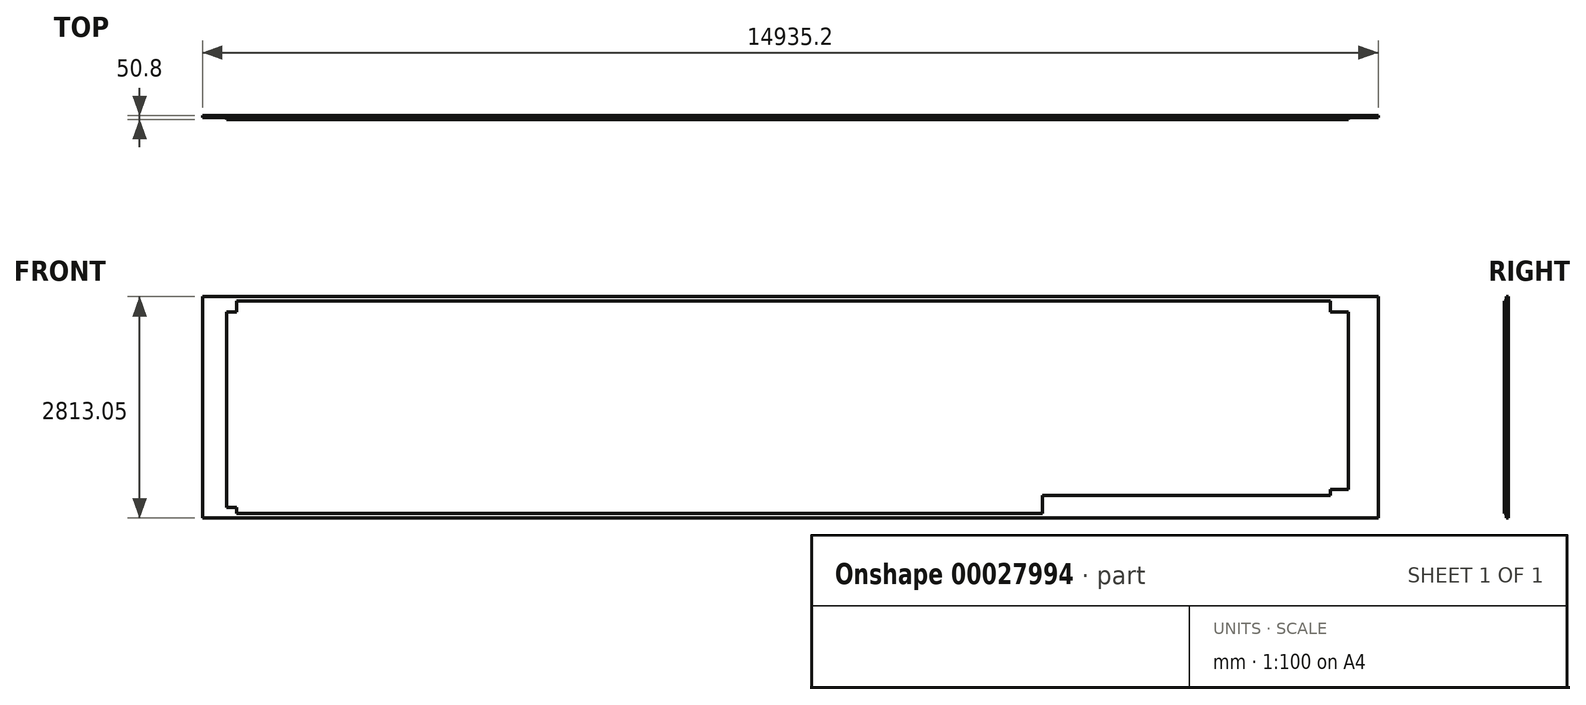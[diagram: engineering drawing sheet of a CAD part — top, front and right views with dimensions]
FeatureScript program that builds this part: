
annotation { "Feature Type Name" : "Feature", "Feature Type Description" : "" }
export const myFeature = defineFeature(function(context is Context, id is Id, definition is map)
    precondition{}
    {
        {
            var Q0;
            Q0=qCreatedBy(makeId("Front.planeOp"),FACE);
            var sketch = newSketch(context, id + "F0", { "sketchPlane" : qUnion([Q0])});
            skLineSegment(sketch, "E0", {"start": v(0, 0) * mm, "end": v(127, 0) * mm});
            skLineSegment(sketch, "E1", {"start": v(127, 0) * mm, "end": v(127, -76.2) * mm});
            skLineSegment(sketch, "E2", {"start": v(127, -76.2) * mm, "end": v(10363.2, -76.2) * mm});
            skLineSegment(sketch, "E3", {"start": v(10363.2, -76.2) * mm, "end": v(10363.2, 152.4) * mm});
            skLineSegment(sketch, "E4", {"start": v(10363.2, 152.4) * mm, "end": v(14020.8, 152.4) * mm});
            skLineSegment(sketch, "E5", {"start": v(14249.4, 228.6) * mm, "end": v(14249.4, 2482.85) * mm});
            skLineSegment(sketch, "E6", {"start": v(14249.4, 2482.85) * mm, "end": v(14020.8, 2482.85) * mm});
            skLineSegment(sketch, "E7", {"start": v(14020.8, 2482.85) * mm, "end": v(14020.8, 2622.55) * mm});
            skLineSegment(sketch, "E8", {"start": v(14020.8, 2622.55) * mm, "end": v(127, 2622.55) * mm});
            skLineSegment(sketch, "E9", {"start": v(127, 2622.55) * mm, "end": v(127, 2482.85) * mm});
            skLineSegment(sketch, "E10", {"start": v(127, 2482.85) * mm, "end": v(0, 2482.85) * mm});
            skLineSegment(sketch, "E11", {"start": v(0, 2482.85) * mm, "end": v(0, 0) * mm});
            skLineSegment(sketch, "E12", {"start": v(14020.8, 152.4) * mm, "end": v(14020.8, 228.6) * mm});
            skLineSegment(sketch, "E13", {"start": v(14020.8, 228.6) * mm, "end": v(14249.4, 228.6) * mm});
            skSolve(sketch);
        }
        {
            var Q0;
            Q0 = qSketchRegion(id + "F0", true);
            extrude(context, id + "F1", {"entities" : qUnion([Q0]), "depth" : 25.4 * mm});
        }
        {
            var Q0;
            Q0=qCreatedBy(makeId("Front.planeOp"),FACE);
            var sketch = newSketch(context, id + "F2", { "sketchPlane" : qUnion([Q0])});
            skLineSegment(sketch, "E14.bottom", {"start": v(-304.8, -133.35) * mm, "end": v(14630.4, -133.35) * mm});
            skLineSegment(sketch, "E14.top", {"start": v(-304.8, 2679.7) * mm, "end": v(14630.4, 2679.7) * mm});
            skLineSegment(sketch, "E14.left", {"start": v(-304.8, -133.35) * mm, "end": v(-304.8, 2679.7) * mm});
            skLineSegment(sketch, "E14.right", {"start": v(14630.4, -133.35) * mm, "end": v(14630.4, 2679.7) * mm});
            skLineSegment(sketch, "E15", {"start": v(10420.35, -133.35) * mm, "end": v(10420.35, 95.25) * mm});
            skLineSegment(sketch, "E16", {"start": v(10420.35, 95.25) * mm, "end": v(14071.6, 95.25) * mm});
            skLineSegment(sketch, "E17", {"start": v(14071.6, 95.25) * mm, "end": v(14071.6, 177.8) * mm});
            skLineSegment(sketch, "E18", {"start": v(14071.6, 177.8) * mm, "end": v(14542.17, 177.8) * mm});
            skLineSegment(sketch, "E19", {"start": v(13868.4, -133.35) * mm, "end": v(13868.4, 2679.7) * mm});
            skLineSegment(sketch, "E20", {"start": v(14071.6, 2679.7) * mm, "end": v(14071.6, 2533.65) * mm});
            skLineSegment(sketch, "E21", {"start": v(14071.6, 2533.65) * mm, "end": v(14630.4, 2533.65) * mm});
            skLineSegment(sketch, "E22", {"start": v(10420.35, 95.25) * mm, "end": v(10362.97, 150.9) * mm});
            skLineSegment(sketch, "E23", {"start": v(14071.6, 2533.65) * mm, "end": v(14024.58, 2483.3) * mm});
            skSolve(sketch);
        }
        {
            var Q0;
            Q0 = qSketchRegion(id + "F2", true);
            extrude(context, id + "F3", {"entities" : qUnion([Q0]), "operationType" : NewBodyOperationType.ADD, "oppositeDirection" : true, "depth" : 25.4 * mm});
        }
    });
